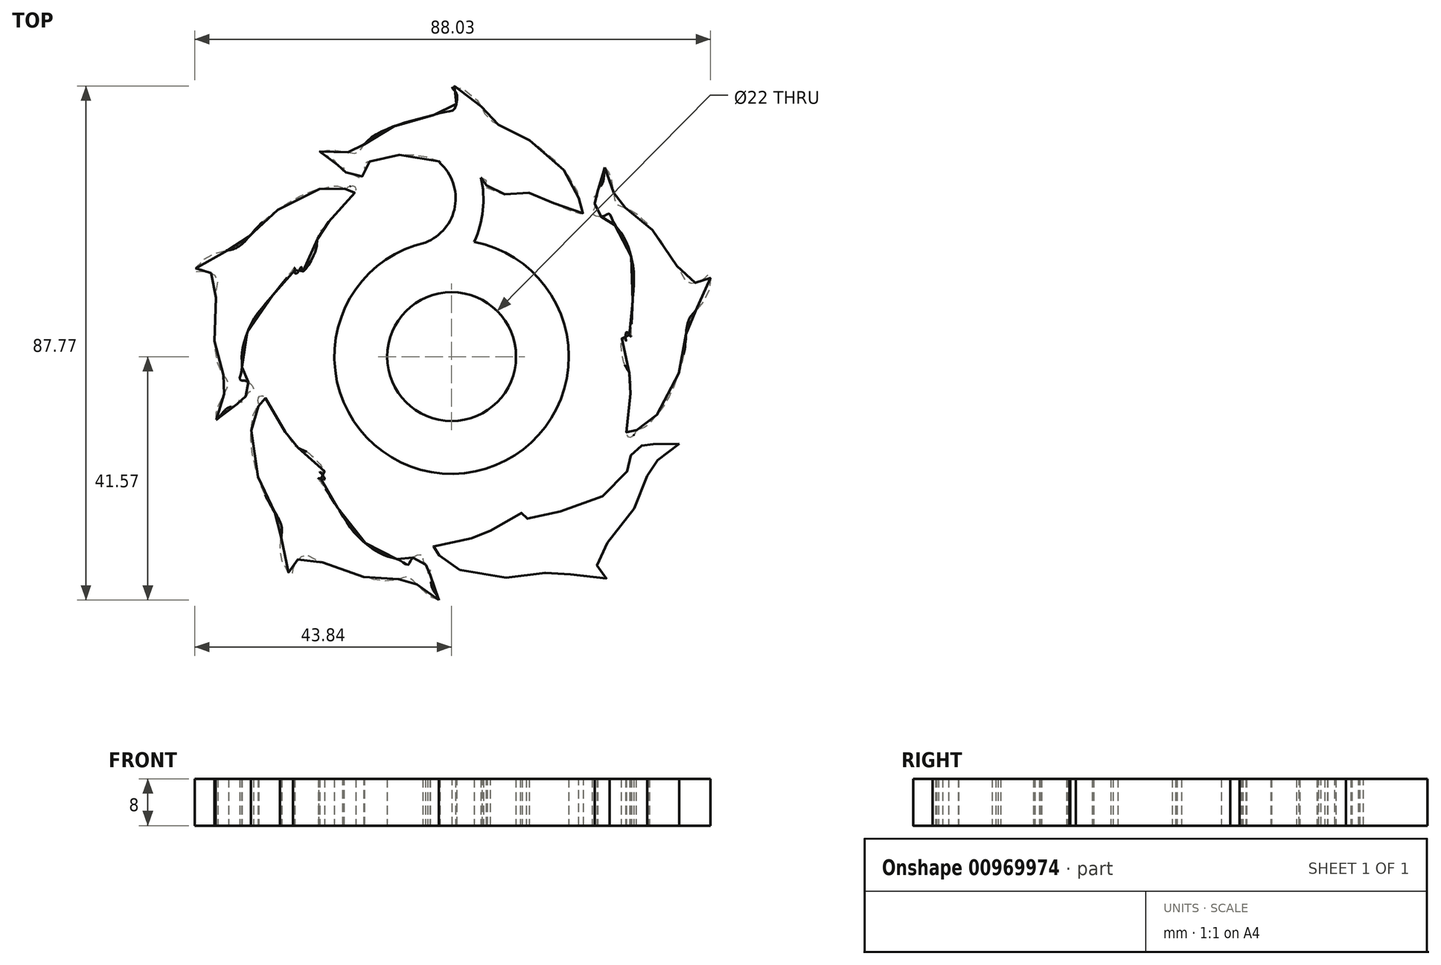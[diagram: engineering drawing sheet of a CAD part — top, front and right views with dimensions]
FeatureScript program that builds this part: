
annotation { "Feature Type Name" : "Feature", "Feature Type Description" : "" }
export const myFeature = defineFeature(function(context is Context, id is Id, definition is map)
    precondition{}
    {
        {
            var Q0;
            Q0=qCreatedBy(makeId("Top.planeOp"),FACE);
            var sketch = newSketch(context, id + "F0", { "sketchPlane" : qUnion([Q0])});
            skCircle(sketch, "E0", {"center": v(0, 0) * mm, "radius": 11 * mm});
            skCircle(sketch, "E1", {"center": v(0, 0) * mm, "radius": 45 * mm, "construction": true});
            skFitSpline(sketch, "E2", {"points": [v(150.16, -25.48) * mm, v(151.18, -25.14) * mm, v(152.93, -25.14) * mm, v(155.19, -25.48) * mm, v(156.38, -25.6) * mm, v(156.9, -25.48) * mm, v(157.36, -24.88) * mm, v(158.64, -23.3) * mm, v(161.2, -21.77) * mm, v(164.36, -20.53) * mm, v(168.83, -19.34) * mm, v(171.99, -18.53) * mm, v(173.14, -18.27) * mm, v(173.65, -17.04) * mm, v(173.65, -15.42) * mm, v(172.97, -14.48) * mm, v(172.97, -14.22) * mm, v(173.82, -14.22) * mm, v(176.55, -15.84) * mm, v(178.3, -18.44) * mm, v(179, -19.55) * mm, v(180.16, -20.46) * mm, v(181.96, -21.27) * mm, v(184.77, -22.6) * mm, v(188.52, -25.16) * mm, v(192.2, -28.82) * mm, v(194.07, -31.83) * mm, v(194.47, -32.84) * mm, v(194.5, -33.94) * mm, v(194.52, -34.26) * mm, v(195.08, -34.8) * mm, v(195.35, -35.58) * mm, v(195.03, -35.96) * mm, v(194.28, -35.93) * mm, v(190.9, -34.47) * mm, v(188.01, -33.16) * mm, v(186.66, -32.67) * mm, v(185.99, -32.35) * mm, v(185.54, -32.3) * mm, v(184.3, -32.47) * mm, v(182.36, -32.66) * mm, v(178.8, -31.64) * mm, v(179.47, -31.25) * mm, v(178.7, -31.05) * mm, v(178.06, -30.58) * mm, v(178.78, -30.31) * mm, v(178.97, -30.15) * mm, v(178.6, -30) * mm, v(172.81, -27.83) * mm, v(168.55, -26.3) * mm, v(164.14, -25.9) * mm, v(161.37, -26.4) * mm, v(159.55, -27.01) * mm, v(158.13, -27.11) * mm, v(157.88, -27.37) * mm, v(158, -28.08) * mm, v(157.67, -29.42) * mm, v(156.86, -29.95) * mm, v(156.47, -29.48) * mm, v(155.92, -29.12) * mm, v(154.59, -28.82) * mm, v(154.27, -28.6) * mm, v(154.31, -28.38) * mm, v(154.5, -28.19) * mm, v(154.44, -28.13) * mm, v(153.92, -28.1) * mm, v(152.98, -27.1) * mm, v(151.89, -26.25) * mm, v(150.16, -25.48) * mm]});
            skCircle(sketch, "E3", {"center": v(0, 0) * mm, "radius": 20 * mm});
            skArc(sketch, "E4", {"start": v(-4.45, 19.5) * mm, "mid": v(0.58, 25.63) * mm, "end": v(-2.05, 33.1) * mm});
            skArc(sketch, "E5", {"start": v(3.88, 19.62) * mm, "mid": v(4.25, 25.84) * mm, "end": v(1.94, 31.63) * mm});
            skArc(sketch, "E6", {"start": v(1.94, 31.63) * mm, "mid": v(0, 32.52) * mm, "end": v(-2.05, 33.1) * mm});
            skLineSegment(sketch, "E7", {"start": v(0, 32.52) * mm, "end": v(172.81, -27.83) * mm, "construction": true});
            skPoint(sketch, "E7.startSnap0", {"position": v(0, 32.52) * mm});
            skArc(sketch, "E8", {"start": v(3.88, 19.62) * mm, "mid": v(5.43, 26.45) * mm, "end": v(4.17, 33.35) * mm});
            skArc(sketch, "E9", {"start": v(4.17, 33.35) * mm, "mid": v(0.98, 35.44) * mm, "end": v(-2.05, 33.1) * mm});
            skSolve(sketch);
        }
        {
            var Q0;
            Q0=makeQuery(id+"F0.imprint","IMPRINT",FACE,{"disambiguationData":[TD([[makeQuery(id+"F0.imprint","IMPRINT",EDGE,{"derivedFrom":sQuery(id+"F0.wireOp",EDGE,"E2")}),-1.0]])]});
            var Q1;
            Q1=makeQuery(id+"F0.imprint","IMPRINT",FACE,{"disambiguationData":[TD([[makeQuery(id+"F0.imprint","IMPRINT",EDGE,{"derivedFrom":sQuery(id+"F0.wireOp",EDGE,"E0")}),-1.0]])]});
            var Q2;
            {var subQ0=sQuery(id+"F0.wireOp",EDGE,"E4");Q2=makeQuery(id+"F0.imprint","IMPRINT",FACE,{"disambiguationData":[TD([[makeQuery(id+"F0.imprint","IMPRINT",EDGE,{"derivedFrom":subQ0}),-1.0]])]});}
            var Q3;
            Q3=makeQuery(id+"F0.imprint","IMPRINT",FACE,{"disambiguationData":[TD([[makeQuery(id+"F0.imprint","IMPRINT",EDGE,{"derivedFrom":sQuery(id+"F0.wireOp",EDGE,"E5")}),-1.0]])]});
            extrude(context, id + "F1", {"entities" : qUnion([Q0, Q1, Q2, Q3]), "depth" : 8 * mm, "offsetDistance" : 25 * mm});
        }
        {
            var Q0;
            Q0=makeQuery(id+"F1.opExtrude","SWEPT_BODY",BODY,{"disambiguationData":[OSD([sQuery(id+"F0.wireOp",EDGE,"E2")])]});
            var Q1;
            Q1=sQuery(id+"F0.wireOp",VERTEX,"E7.startSnap0");
            var Q2;
            Q2=sQuery(id+"F0.wireOp",VERTEX,"E7.end");
            transform(context, id + "F2", {"entities" : qUnion([Q0]), "transformType" : TransformType.TRANSLATION_ENTITY, "oppositeDirectionEntity" : true, "transformLine" : qUnion([Q1, Q2]), "makeCopy" : false});
        }
        {
            var Q0;
            Q0=makeQuery(id+"F1.opExtrude","SWEPT_BODY",BODY,{"disambiguationData":[OSD([sQuery(id+"F0.wireOp",EDGE,"E2")])]});
            var Q1;
            Q1=sQuery(id+"F0.wireOp",EDGE,"E0");
            circularPattern(context, id + "F3", {"operationType" : NewBodyOperationType.ADD, "entities" : qUnion([Q0]), "axis" : qUnion([Q1]), "angle" : 360 * degree, "instanceCount" : 5, "equalSpace" : true});
        }
    });
